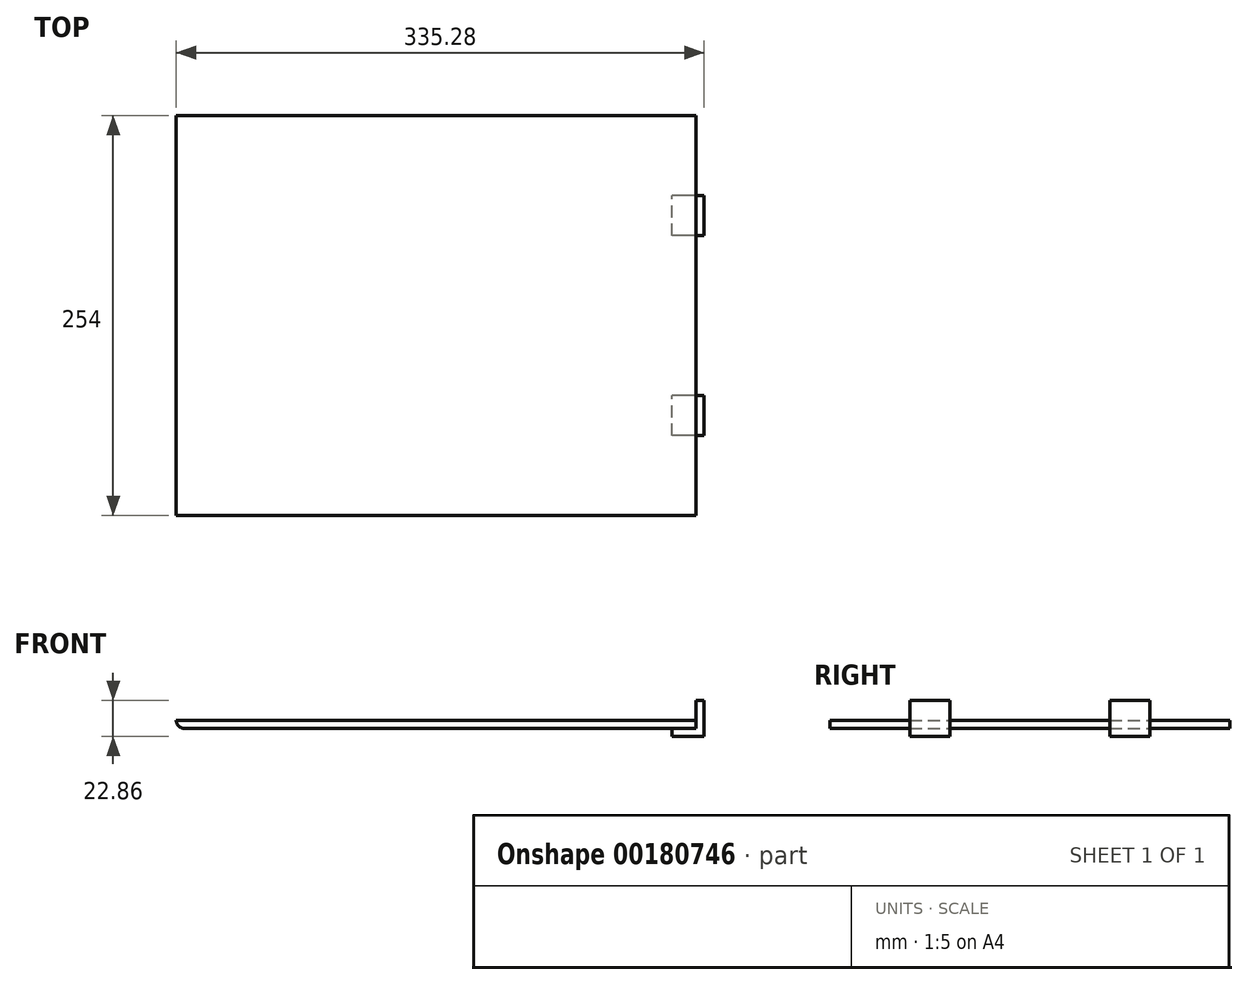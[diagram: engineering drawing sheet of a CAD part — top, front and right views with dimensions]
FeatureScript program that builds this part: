
annotation { "Feature Type Name" : "Feature", "Feature Type Description" : "" }
export const myFeature = defineFeature(function(context is Context, id is Id, definition is map)
    precondition{}
    {
        {
            var Q0;
            Q0=qCreatedBy(makeId("Front.planeOp"),FACE);
            var sketch = newSketch(context, id + "F0", { "sketchPlane" : qUnion([Q0])});
            skLineSegment(sketch, "E0", {"start": v(-160.03, 0) * mm, "end": v(170.17, 0) * mm});
            skLineSegment(sketch, "E1", {"start": v(170.17, 0) * mm, "end": v(170.17, -5.08) * mm});
            skLineSegment(sketch, "E2", {"start": v(170.17, -5.08) * mm, "end": v(-160.03, -5.08) * mm});
            skLineSegment(sketch, "E3", {"start": v(-160.03, 0) * mm, "end": v(-160.03, -5.08) * mm});
            skSolve(sketch);
        }
        {
            var Q0;
            Q0=makeQuery(id+"F0.imprint","IMPRINT",FACE,{"disambiguationData":[TD([[makeQuery(id+"F0.imprint","IMPRINT",EDGE,{"derivedFrom":sQuery(id+"F0.wireOp",EDGE,"E0")}),-1.0]])]});
            extrude(context, id + "F1", {"entities" : qUnion([Q0]), "depth" : 50.8 * mm});
        }
        {
            var Q0;
            Q0=makeQuery(id+"F1.opExtrude","CAP_FACE",FACE,{"disambiguationData":[OSD([sQuery(id+"F0.wireOp",EDGE,"E0"),sQuery(id+"F0.wireOp",EDGE,"E1"),sQuery(id+"F0.wireOp",EDGE,"E2"),sQuery(id+"F0.wireOp",EDGE,"E3")])],"isStart":false});
            var sketch = newSketch(context, id + "F2", { "sketchPlane" : qUnion([Q0])});
            skLineSegment(sketch, "E4", {"start": v(170.17, 0) * mm, "end": v(170.17, 12.7) * mm});
            skLineSegment(sketch, "E5", {"start": v(170.17, 12.7) * mm, "end": v(175.25, 12.7) * mm});
            skLineSegment(sketch, "E6", {"start": v(175.25, 12.7) * mm, "end": v(175.25, -10.16) * mm});
            skLineSegment(sketch, "E7", {"start": v(175.25, -10.16) * mm, "end": v(154.93, -10.16) * mm});
            skLineSegment(sketch, "E8", {"start": v(154.93, -10.16) * mm, "end": v(154.93, -5.08) * mm});
            skSolve(sketch);
        }
        {
            var Q0;
            Q0=makeQuery(id+"F2.imprint","IMPRINT",FACE,{"disambiguationData":[TD([[makeQuery(id+"F2.imprint","IMPRINT",EDGE,{"derivedFrom":makeQuery(id+"F1.opExtrude","CAP_EDGE",EDGE,{"disambiguationData":[OSD([sQuery(id+"F0.wireOp",EDGE,"E0")])],"isStart":false})}),-1.0]])]});
            var Q1;
            Q1=makeQuery(id+"F2.imprint","IMPRINT",FACE,{"disambiguationData":[TD([[makeQuery(id+"F2.imprint","IMPRINT",EDGE,{"derivedFrom":sQuery(id+"F2.wireOp",EDGE,"E4")}),-1.0]])]});
            extrude(context, id + "F3", {"entities" : qUnion([Q0, Q1]), "operationType" : NewBodyOperationType.ADD, "depth" : 25.4 * mm});
        }
        {
            var Q0;
            Q0=makeQuery(id+"F3.opExtrude","CAP_FACE",FACE,{"disambiguationData":[OSD([sQuery(id+"F0.wireOp",EDGE,"E0"),sQuery(id+"F0.wireOp",EDGE,"E2"),sQuery(id+"F0.wireOp",EDGE,"E3"),sQuery(id+"F2.wireOp",EDGE,"E4"),sQuery(id+"F2.wireOp",EDGE,"E5"),sQuery(id+"F2.wireOp",EDGE,"E6"),sQuery(id+"F2.wireOp",EDGE,"E7"),sQuery(id+"F2.wireOp",EDGE,"E8")])],"isStart":false});
            var sketch = newSketch(context, id + "F4", { "sketchPlane" : qUnion([Q0])});
            skLineSegment(sketch, "E9", {"start": v(-160.03, 0) * mm, "end": v(-160.03, -5.08) * mm});
            skLineSegment(sketch, "E10", {"start": v(-160.03, -5.08) * mm, "end": v(170.17, -5.08) * mm});
            skLineSegment(sketch, "E11", {"start": v(170.17, -5.08) * mm, "end": v(170.17, 0) * mm});
            skLineSegment(sketch, "E12", {"start": v(170.17, 0) * mm, "end": v(-160.03, 0) * mm});
            skSolve(sketch);
        }
        {
            var Q0;
            {var subQ2=sQuery(id+"F4.wireOp",EDGE,"E9");Q0=makeQuery(id+"F4.imprint","IMPRINT",FACE,{"disambiguationData":[TD([[makeQuery(id+"F4.imprint","IMPRINT",EDGE,{"derivedFrom":subQ2}),1.0]])]});}
            extrude(context, id + "F5", {"entities" : qUnion([Q0]), "operationType" : NewBodyOperationType.ADD, "depth" : 101.6 * mm});
        }
        {
            var Q0;
            Q0=makeQuery(id+"F5.opExtrude","CAP_FACE",FACE,{"disambiguationData":[OSD([sQuery(id+"F4.wireOp",EDGE,"E9"),sQuery(id+"F4.wireOp",EDGE,"E10"),sQuery(id+"F4.wireOp",EDGE,"E11"),sQuery(id+"F4.wireOp",EDGE,"E12")])],"isStart":false});
            var sketch = newSketch(context, id + "F6", { "sketchPlane" : qUnion([Q0])});
            skLineSegment(sketch, "E13", {"start": v(170.17, 0) * mm, "end": v(170.17, 12.7) * mm});
            skLineSegment(sketch, "E14", {"start": v(170.17, 12.7) * mm, "end": v(175.25, 12.7) * mm});
            skLineSegment(sketch, "E15", {"start": v(175.25, 12.7) * mm, "end": v(175.25, -10.16) * mm});
            skLineSegment(sketch, "E16", {"start": v(175.25, -10.16) * mm, "end": v(154.93, -10.16) * mm});
            skLineSegment(sketch, "E17", {"start": v(154.93, -10.16) * mm, "end": v(154.93, -5.08) * mm});
            skSolve(sketch);
        }
        {
            var Q0;
            {var subQ1=makeQuery(id+"F5.opExtrude","CAP_EDGE",EDGE,{"disambiguationData":[OSD([sQuery(id+"F4.wireOp",EDGE,"E9")])],"isStart":false});Q0=makeQuery(id+"F6.imprint","IMPRINT",FACE,{"disambiguationData":[TD([[makeQuery(id+"F6.imprint","IMPRINT",EDGE,{"derivedFrom":subQ1}),1.0]])]});}
            var Q1;
            Q1=makeQuery(id+"F6.imprint","IMPRINT",FACE,{"disambiguationData":[TD([[makeQuery(id+"F6.imprint","IMPRINT",EDGE,{"derivedFrom":sQuery(id+"F6.wireOp",EDGE,"E13")}),-1.0]])]});
            extrude(context, id + "F7", {"entities" : qUnion([Q0, Q1]), "operationType" : NewBodyOperationType.ADD, "depth" : 25.4 * mm});
        }
        {
            var Q0;
            Q0=makeQuery(id+"F7.opExtrude","CAP_FACE",FACE,{"disambiguationData":[OSD([sQuery(id+"F4.wireOp",EDGE,"E9"),sQuery(id+"F4.wireOp",EDGE,"E10"),sQuery(id+"F4.wireOp",EDGE,"E12"),sQuery(id+"F6.wireOp",EDGE,"E13"),sQuery(id+"F6.wireOp",EDGE,"E14"),sQuery(id+"F6.wireOp",EDGE,"E15"),sQuery(id+"F6.wireOp",EDGE,"E16"),sQuery(id+"F6.wireOp",EDGE,"E17")])],"isStart":false});
            var sketch = newSketch(context, id + "F8", { "sketchPlane" : qUnion([Q0])});
            skLineSegment(sketch, "E18", {"start": v(-160.03, 0) * mm, "end": v(-160.03, -5.08) * mm});
            skLineSegment(sketch, "E19", {"start": v(-160.03, -5.08) * mm, "end": v(170.17, -5.08) * mm});
            skLineSegment(sketch, "E20", {"start": v(170.17, -5.08) * mm, "end": v(170.17, 0) * mm});
            skLineSegment(sketch, "E21", {"start": v(170.17, 0) * mm, "end": v(-160.03, 0) * mm});
            skSolve(sketch);
        }
        {
            var Q0;
            {var subQ3=sQuery(id+"F8.wireOp",EDGE,"E18");Q0=makeQuery(id+"F8.imprint","IMPRINT",FACE,{"disambiguationData":[TD([[makeQuery(id+"F8.imprint","IMPRINT",EDGE,{"derivedFrom":subQ3}),1.0]])]});}
            extrude(context, id + "F9", {"entities" : qUnion([Q0]), "operationType" : NewBodyOperationType.ADD, "depth" : 50.8 * mm});
        }
        {
            var Q0;
            {var subQ0=sQuery(id+"F4.wireOp",EDGE,"E10");var subQ1=sQuery(id+"F4.wireOp",EDGE,"E9");var subQ2=sQuery(id+"F0.wireOp",EDGE,"E3");var subQ3=sQuery(id+"F0.wireOp",EDGE,"E2");Q0=makeQuery(id+"F9.boolean.opBoolean","MERGE",EDGE,{"derivedFrom":[makeQuery(id+"F7.boolean.opBoolean","MERGE",EDGE,{"derivedFrom":[makeQuery(id+"F5.boolean.opBoolean","MERGE",EDGE,{"derivedFrom":[makeQuery(id+"F3.boolean.opBoolean","MERGE",EDGE,{"derivedFrom":[makeQuery(id+"F1.opExtrude","SWEPT_EDGE",EDGE,{"disambiguationData":[OSD([subQ3,subQ2])]}),makeQuery(id+"F3.opExtrude","SWEPT_EDGE",EDGE,{"disambiguationData":[OSD([subQ3,subQ2])]})]}),makeQuery(id+"F5.opExtrude","SWEPT_EDGE",EDGE,{"disambiguationData":[OSD([subQ1,subQ0])]})]}),makeQuery(id+"F7.opExtrude","SWEPT_EDGE",EDGE,{"disambiguationData":[OSD([subQ1,subQ0])]})]}),makeQuery(id+"F9.opExtrude","SWEPT_EDGE",EDGE,{"disambiguationData":[OSD([sQuery(id+"F8.wireOp",EDGE,"E18"),sQuery(id+"F8.wireOp",EDGE,"E19")])]})]});}
            fillet(context, id + "F10", {"entities" : qUnion([Q0]), "radius" : 5.08 * mm, "tangentPropagation" : true, "allowEdgeOverflow" : false});
        }
    });
